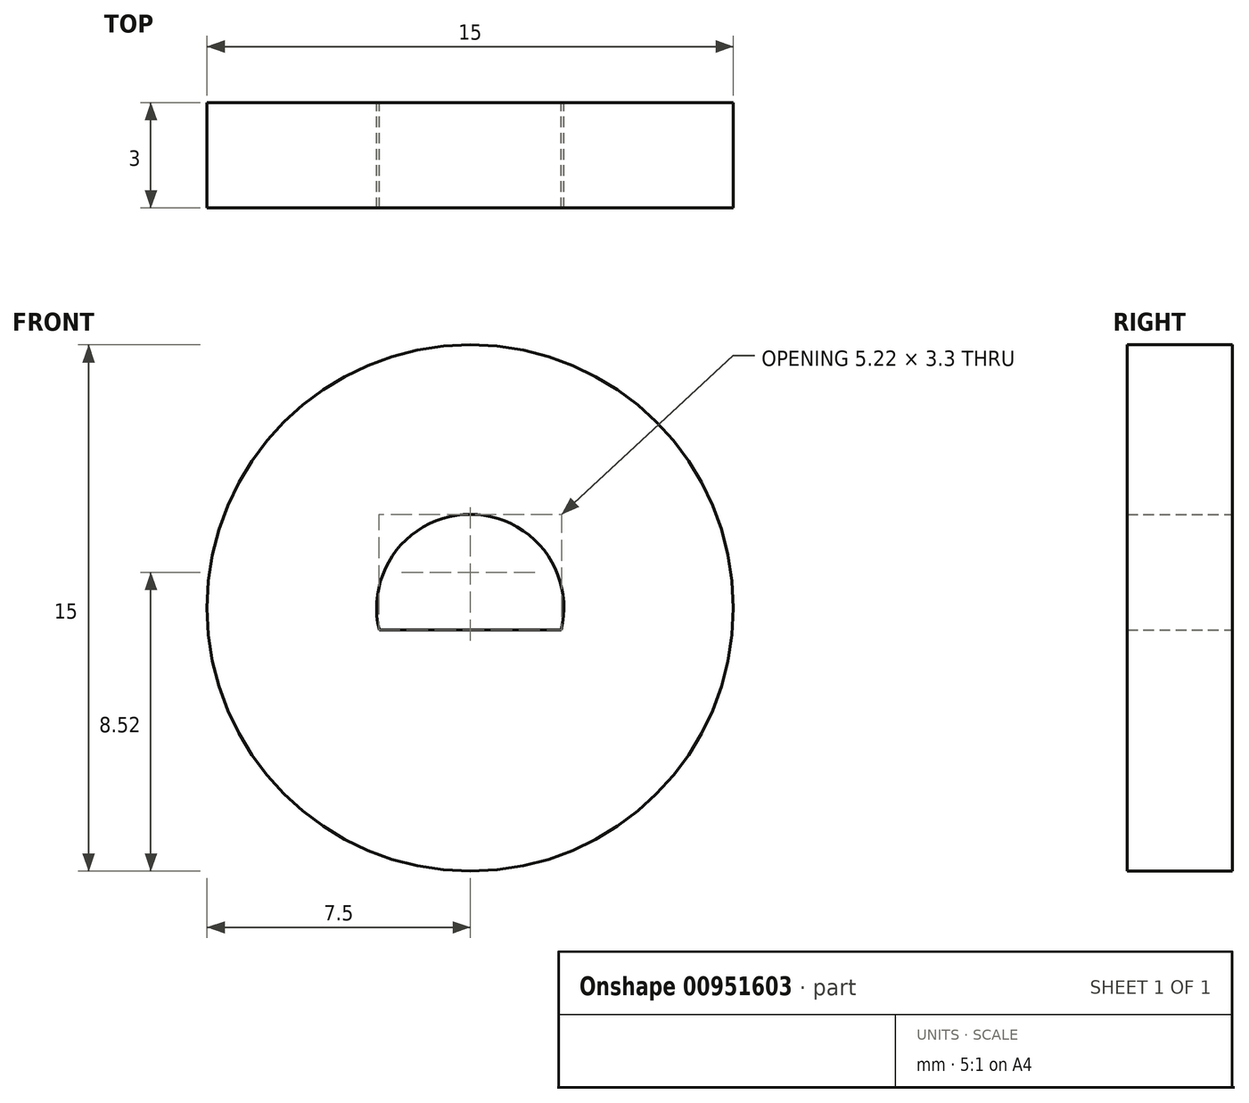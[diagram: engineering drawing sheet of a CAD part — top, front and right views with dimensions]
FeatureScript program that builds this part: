
annotation { "Feature Type Name" : "Feature", "Feature Type Description" : "" }
export const myFeature = defineFeature(function(context is Context, id is Id, definition is map)
    precondition{}
    {
        {
            var Q0;
            Q0=qCreatedBy(makeId("Front.planeOp"),FACE);
            var sketch = newSketch(context, id + "F0", { "sketchPlane" : qUnion([Q0])});
            skCircle(sketch, "E0", {"center": v(0, 0) * mm, "radius": 7.5 * mm});
            skLineSegment(sketch, "E1", {"start": v(0, 2.67) * mm, "end": v(0, -0.63) * mm, "construction": true});
            skLineSegment(sketch, "E2", {"start": v(0, -0.63) * mm, "end": v(2.6, -0.63) * mm});
            skLineSegment(sketch, "E3.MirrorCS", {"start": v(0, -0.63) * mm, "end": v(-2.6, -0.63) * mm});
            skArc(sketch, "E4", {"start": v(2.6, -0.63) * mm, "mid": v(0, 2.67) * mm, "end": v(-2.6, -0.63) * mm});
            skPoint(sketch, "E5", {"position": v(0, 2.67) * mm});
            skSolve(sketch);
        }
        {
            var Q0;
            Q0=qSketchRegion(id+"F0",true);
            extrude(context, id + "F1", {"entities" : qUnion([Q0]), "depth" : 3 * mm, "offsetDistance" : 25 * mm});
        }
    });
